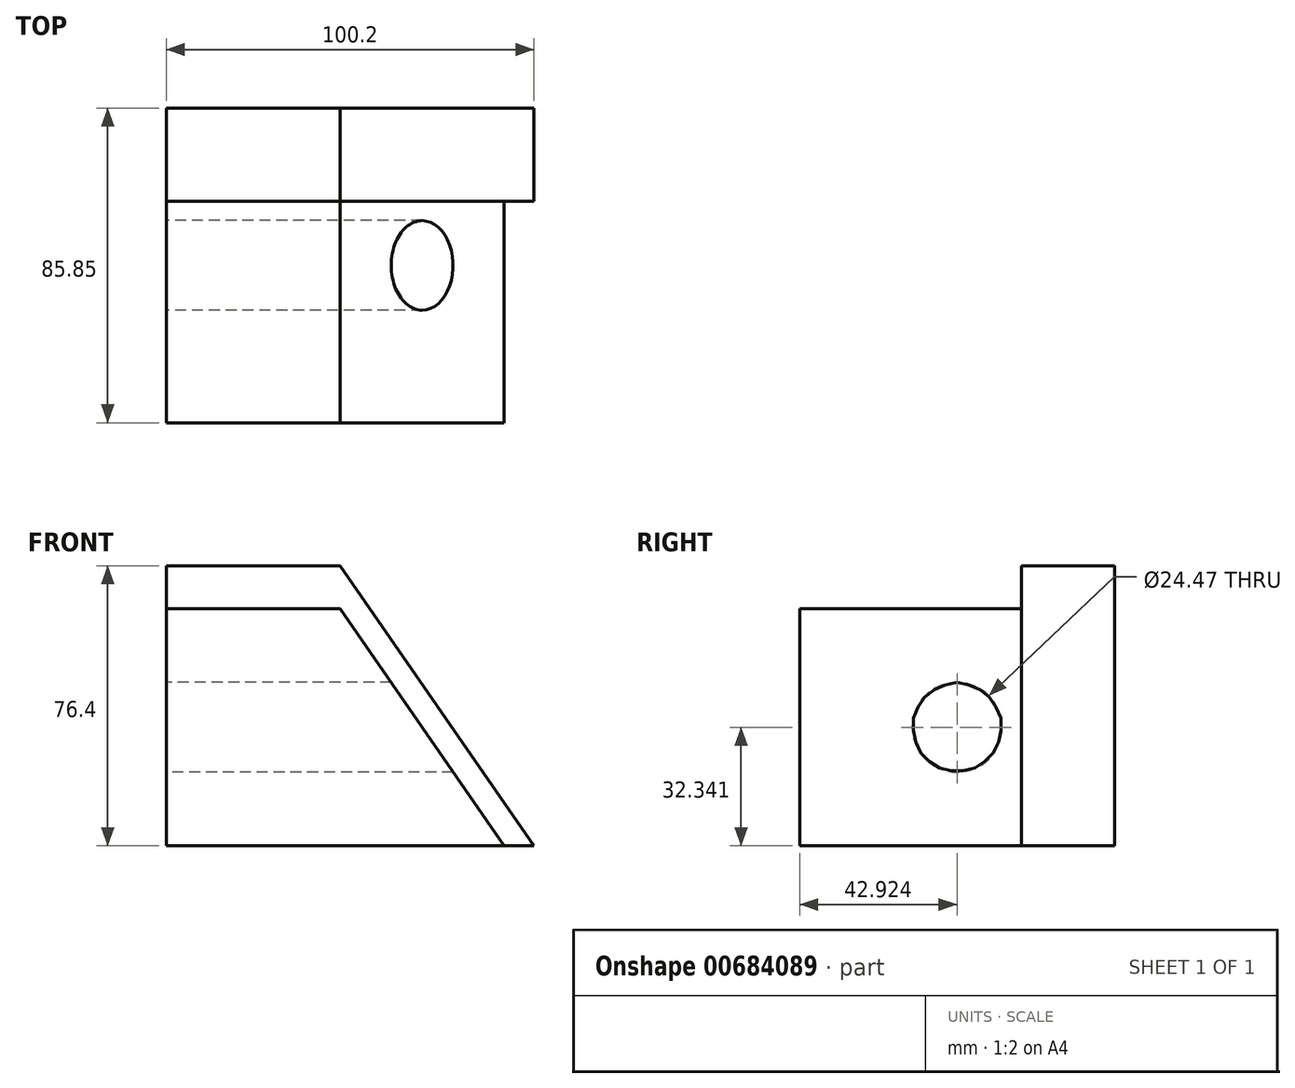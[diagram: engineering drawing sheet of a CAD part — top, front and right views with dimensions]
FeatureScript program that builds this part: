
annotation { "Feature Type Name" : "Feature", "Feature Type Description" : "" }
export const myFeature = defineFeature(function(context is Context, id is Id, definition is map)
    precondition{}
    {
        {
            var Q0;
            Q0=qCreatedBy(makeId("Front.planeOp"),FACE);
            var sketch = newSketch(context, id + "F0", { "sketchPlane" : qUnion([Q0])});
            skLineSegment(sketch, "E0", {"start": v(0, 0) * mm, "end": v(-44.7, 64.68) * mm});
            skLineSegment(sketch, "E1", {"start": v(-44.7, 64.68) * mm, "end": v(-92.1, 64.68) * mm});
            skLineSegment(sketch, "E2", {"start": v(-92.1, 64.68) * mm, "end": v(-92.1, 0) * mm});
            skLineSegment(sketch, "E3", {"start": v(-92.1, 0) * mm, "end": v(0, 0) * mm});
            skSolve(sketch);
        }
        {
            var Q0;
            Q0 = qSketchRegion(id + "F0", true);
            extrude(context, id + "F1", {"entities" : qUnion([Q0]), "depth" : 85.85 * mm, "offsetDistance" : 25.4 * mm});
        }
        {
            var Q0;
            Q0=makeQuery(id+"F1.opExtrude","CAP_FACE",FACE,{"disambiguationData":[OSD([sQuery(id+"F0.wireOp",EDGE,"E0"),sQuery(id+"F0.wireOp",EDGE,"E1"),sQuery(id+"F0.wireOp",EDGE,"E2"),sQuery(id+"F0.wireOp",EDGE,"E3")])],"isStart":true});
            var sketch = newSketch(context, id + "F2", { "sketchPlane" : qUnion([Q0])});
            skLineSegment(sketch, "E4", {"start": v(92.1, 64.68) * mm, "end": v(92.1, 76.4) * mm});
            skLineSegment(sketch, "E5", {"start": v(92.1, 76.4) * mm, "end": v(44.7, 76.4) * mm});
            skLineSegment(sketch, "E6", {"start": v(44.7, 76.4) * mm, "end": v(-8.1, 0) * mm});
            skLineSegment(sketch, "E7", {"start": v(-8.1, 0) * mm, "end": v(0, 0) * mm});
            skLineSegment(sketch, "E8", {"start": v(0, 0) * mm, "end": v(44.7, 64.68) * mm});
            skLineSegment(sketch, "E9", {"start": v(44.7, 64.68) * mm, "end": v(92.1, 64.68) * mm});
            skSolve(sketch);
        }
        {
            var Q0;
            Q0 = qSketchRegion(id + "F2", true);
            extrude(context, id + "F3", {"entities" : qUnion([Q0]), "operationType" : NewBodyOperationType.ADD, "oppositeDirection" : true, "depth" : 25.4 * mm, "offsetDistance" : 25.4 * mm});
        }
        {
            var Q0;
            Q0=makeQuery(id+"F3.boolean.opBoolean","MERGE",FACE,{"derivedFrom":[makeQuery(id+"F1.opExtrude","SWEPT_FACE",FACE,{"disambiguationData":[OSD([sQuery(id+"F0.wireOp",EDGE,"E2")])]}),makeQuery(id+"F3.opExtrude","SWEPT_FACE",FACE,{"disambiguationData":[OSD([sQuery(id+"F2.wireOp",EDGE,"E4")])]})]});
            var sketch = newSketch(context, id + "F4", { "sketchPlane" : qUnion([Q0])});
            skCircle(sketch, "E10", {"center": v(42.93, 32.34) * mm, "radius": 12.23 * mm});
            skPoint(sketch, "E10.centerSnap0", {"position": v(42.93, 0) * mm});
            skPoint(sketch, "E10.centerSnap1", {"position": v(85.85, 32.34) * mm});
            skSolve(sketch);
        }
        {
            var Q0;
            Q0 = qSketchRegion(id + "F4", true);
            extrude(context, id + "F5", {"entities" : qUnion([Q0]), "operationType" : NewBodyOperationType.REMOVE, "endBound" : BoundingType.THROUGH_ALL, "oppositeDirection" : true, "depth" : 25.4 * mm, "offsetDistance" : 25.4 * mm});
        }
    });
